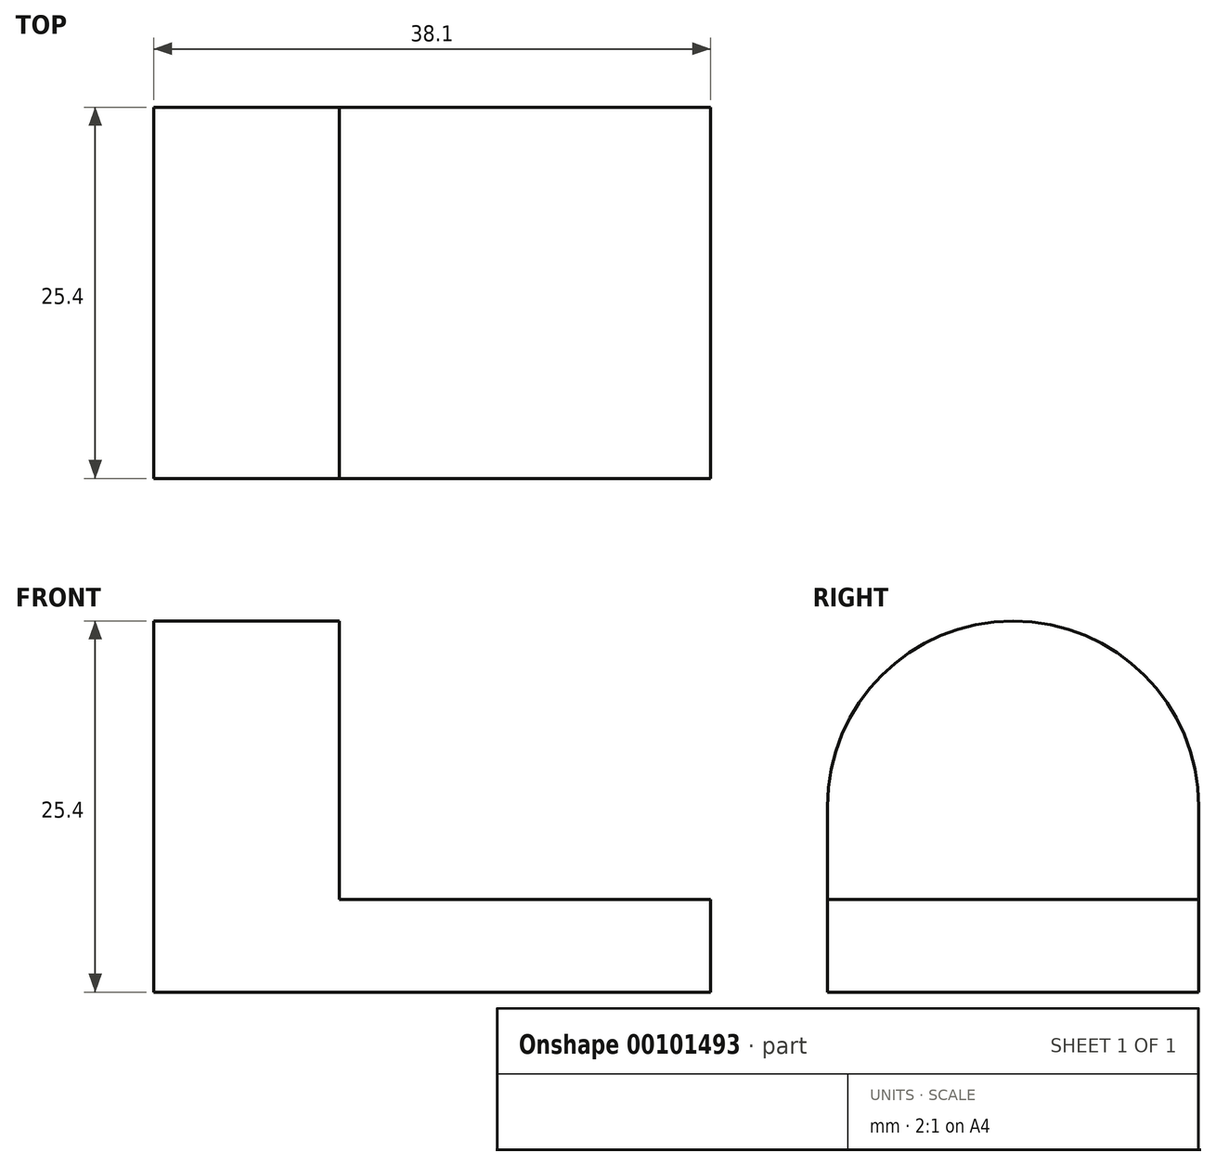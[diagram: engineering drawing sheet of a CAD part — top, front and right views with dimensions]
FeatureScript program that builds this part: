
annotation { "Feature Type Name" : "Feature", "Feature Type Description" : "" }
export const myFeature = defineFeature(function(context is Context, id is Id, definition is map)
    precondition{}
    {
        {
            var Q0;
            Q0=qCreatedBy(makeId("Right.planeOp"),FACE);
            var sketch = newSketch(context, id + "F0", { "sketchPlane" : qUnion([Q0])});
            skLineSegment(sketch, "E0", {"start": v(0, 0) * mm, "end": v(25.4, 0) * mm});
            skLineSegment(sketch, "E1", {"start": v(25.4, 0) * mm, "end": v(25.4, 12.7) * mm});
            skLineSegment(sketch, "E2", {"start": v(25.4, 12.7) * mm, "end": v(25.4, 0) * mm});
            skLineSegment(sketch, "E3", {"start": v(0, 0) * mm, "end": v(0, 12.7) * mm});
            skArc(sketch, "E4", {"start": v(0, 12.7) * mm, "mid": v(12.7, 25.4) * mm, "end": v(25.4, 12.7) * mm});
            skSolve(sketch);
        }
        {
            var Q0;
            Q0=makeQuery(id+"F0.imprint","IMPRINT",FACE,{"disambiguationData":[TD([[makeQuery(id+"F0.imprint","IMPRINT",EDGE,{"derivedFrom":sQuery(id+"F0.wireOp",EDGE,"E0")}),1.0]])]});
            extrude(context, id + "F1", {"entities" : qUnion([Q0]), "depth" : 12.7 * mm});
        }
        {
            var Q0;
            Q0=makeQuery(id+"F1.opExtrude","CAP_FACE",FACE,{"disambiguationData":[OSD([sQuery(id+"F0.wireOp",EDGE,"E0"),sQuery(id+"F0.wireOp",EDGE,"E2"),sQuery(id+"F0.wireOp",EDGE,"E3"),sQuery(id+"F0.wireOp",EDGE,"E4")])],"isStart":false});
            var sketch = newSketch(context, id + "F2", { "sketchPlane" : qUnion([Q0])});
            skLineSegment(sketch, "E5", {"start": v(0, 6.35) * mm, "end": v(25.4, 6.35) * mm});
            skSolve(sketch);
        }
        {
            var Q0;
            {var subQ0=sQuery(id+"F2.wireOp",EDGE,"E5");Q0=makeQuery(id+"F2.imprint","IMPRINT",FACE,{"disambiguationData":[TD([[makeQuery(id+"F2.imprint","IMPRINT",EDGE,{"derivedFrom":subQ0}),-1.0]])]});}
            extrude(context, id + "F3", {"entities" : qUnion([Q0]), "operationType" : NewBodyOperationType.ADD, "depth" : 25.4 * mm});
        }
    });
